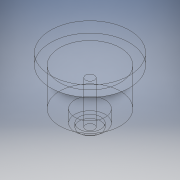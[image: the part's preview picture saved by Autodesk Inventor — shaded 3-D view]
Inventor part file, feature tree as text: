
AUTODESK INVENTOR PART (.ipt)
format: ipt  version: 2018.3 (Build 223285000, 285)  size: 133,632 bytes
history: native  units: mm
features: imported_body x1, extrude x1, thread x1, sketch x1
ambient origin geometry x8: Origin, YZ Plane, XZ Plane, XY Plane, X Axis, Y Axis, Z Axis, Center Point
bodies: Solid1 (feature_tree)
feature tree (4):
  imported_body  "Base1"
  extrude  "Extrusion1"  Depth=10.0mm TaperAngle=0.0deg
  thread  "Thread1"  [1 undecoded]
  sketch  "Sketch1"  dims[d0=2.46mm d1=12.0mm d2=0.0mm d3=10.0mm d4=0.0mm]
note: 1 required parameter value undecoded (feature->parameter linkage not recoverable at this tier; creation-order binding heuristic only, values carry confidence <= 0.55)
